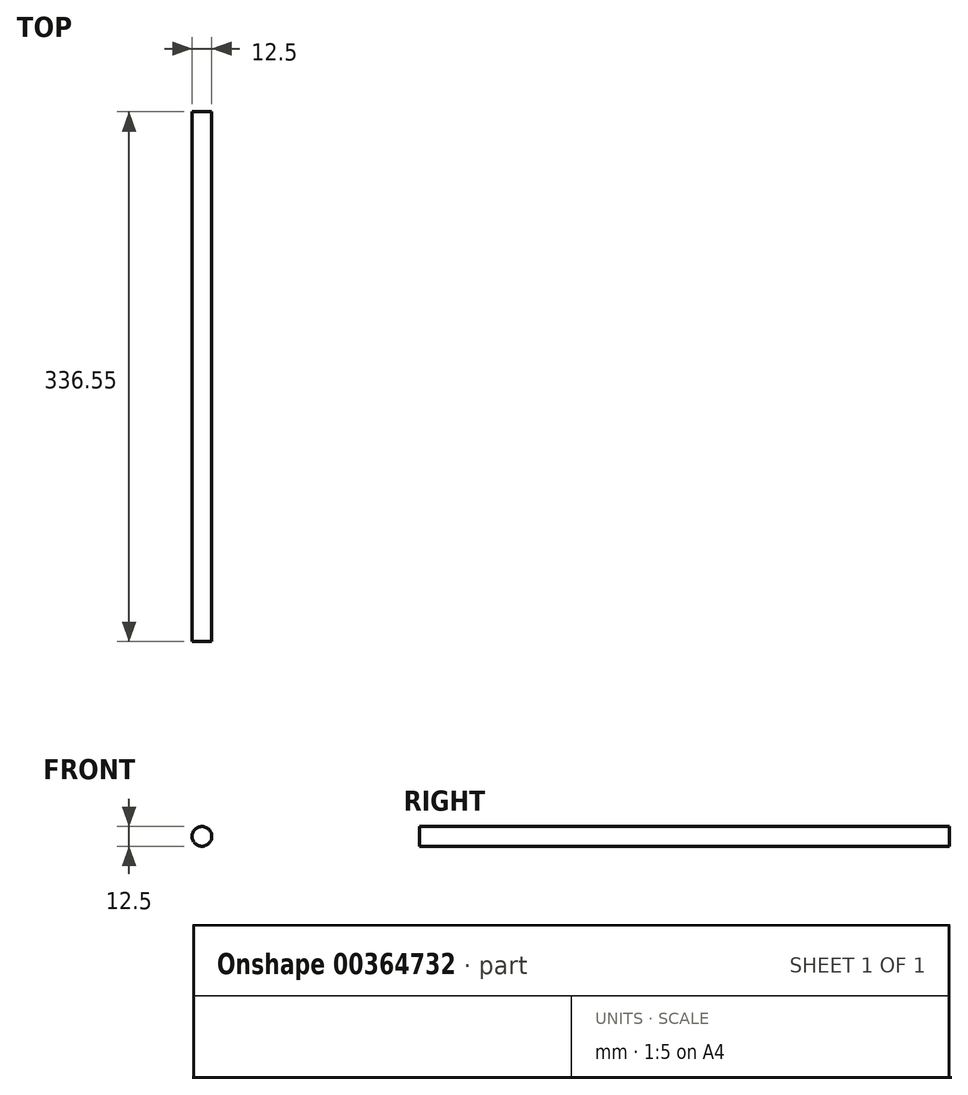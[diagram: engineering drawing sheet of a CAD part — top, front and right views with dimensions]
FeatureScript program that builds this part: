
annotation { "Feature Type Name" : "Feature", "Feature Type Description" : "" }
export const myFeature = defineFeature(function(context is Context, id is Id, definition is map)
    precondition{}
    {
        {
            var Q0;
            Q0=qCreatedBy(makeId("Front.planeOp"),FACE);
            var sketch = newSketch(context, id + "F0", { "sketchPlane" : qUnion([Q0])});
            skCircle(sketch, "E0", {"center": v(0, 0) * mm, "radius": 6.25 * mm});
            skSolve(sketch);
        }
        {
            var Q0;
            Q0=qSketchRegion(id+"F0",true);
            extrude(context, id + "F1", {"entities" : qUnion([Q0]), "depth" : 336.55 * mm});
        }
    });
